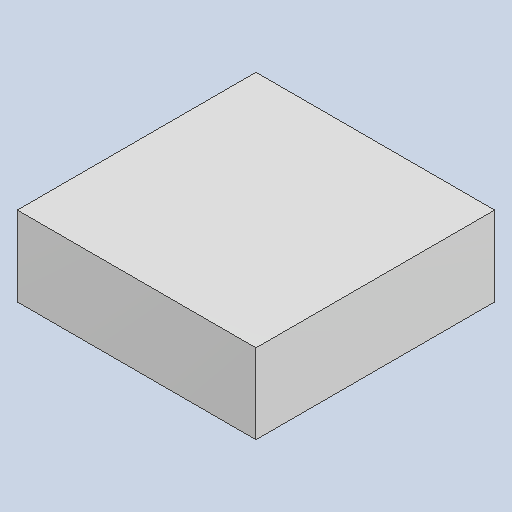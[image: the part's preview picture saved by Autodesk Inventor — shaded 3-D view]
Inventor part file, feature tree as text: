
AUTODESK INVENTOR PART (.ipt)
format: ipt  version: 2023.4 (Build 274418000, 418)  size: 79,872 bytes
history: native  units: mm
features: extrude x1
ambient origin geometry x8: Origin, YZ Plane, XZ Plane, XY Plane, X Axis, Y Axis, Z Axis, Center Point
bodies: Solid1 (feature_tree)
feature tree (1):
  extrude  "Extruded_21"  [1 undecoded]
note: 1 required parameter value undecoded (feature->parameter linkage not recoverable at this tier; creation-order binding heuristic only, values carry confidence <= 0.55)
